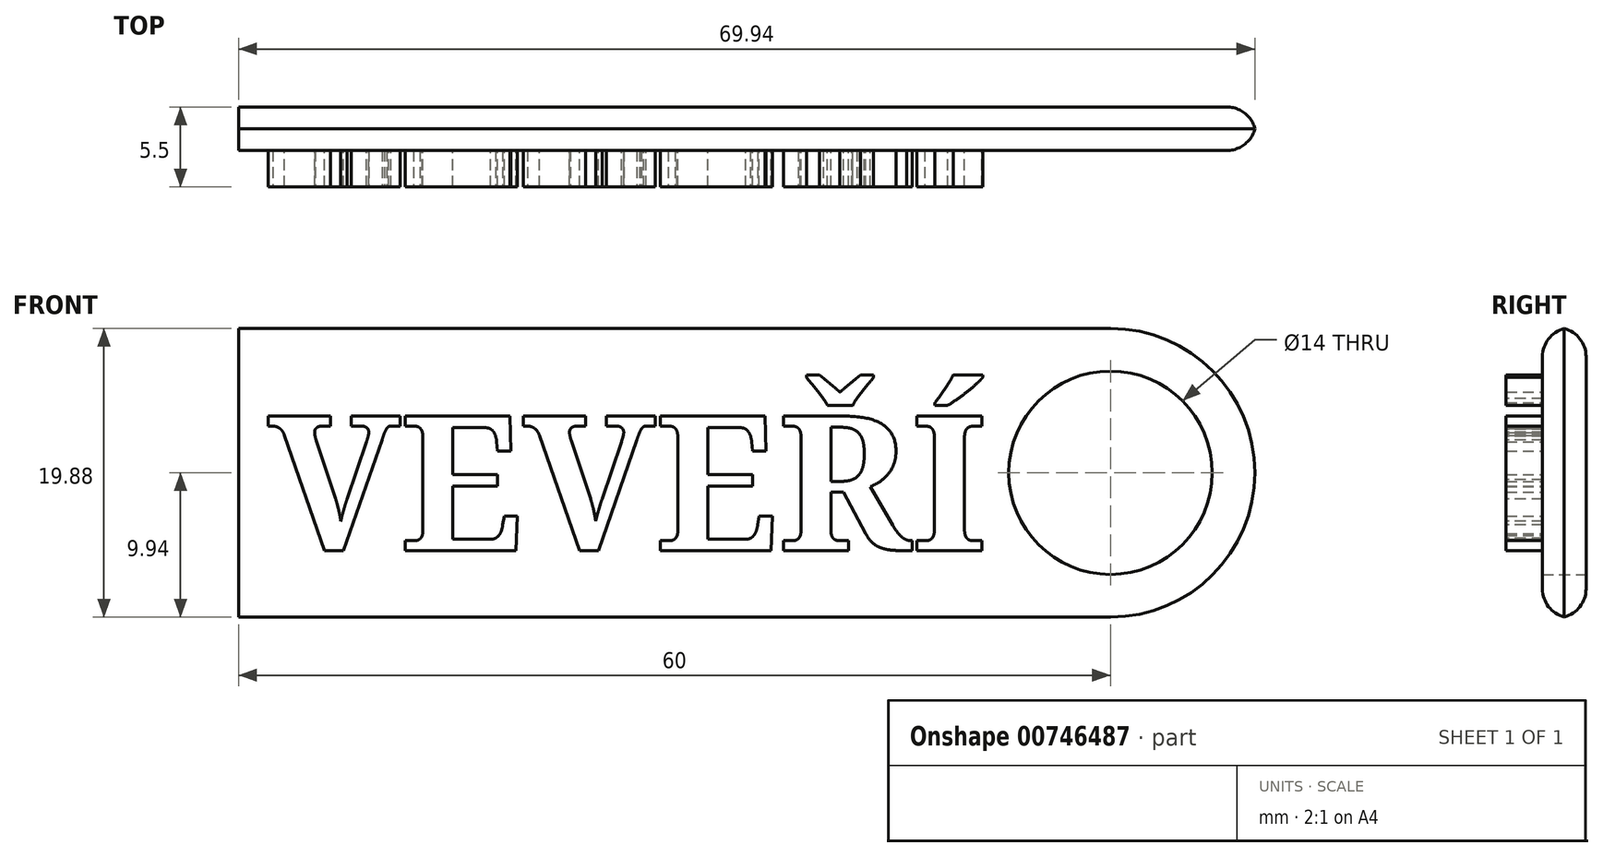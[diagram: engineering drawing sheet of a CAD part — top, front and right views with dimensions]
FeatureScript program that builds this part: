
annotation { "Feature Type Name" : "Feature", "Feature Type Description" : "" }
export const myFeature = defineFeature(function(context is Context, id is Id, definition is map)
    precondition{}
    {
        {
            var Q0;
            Q0=qCreatedBy(makeId("Front.planeOp"),FACE);
            var sketch = newSketch(context, id + "F0", { "sketchPlane" : qUnion([Q0])});
            skLineSegment(sketch, "E0.bottom", {"start": v(-30, 10) * mm, "end": v(30, 10) * mm});
            skLineSegment(sketch, "E0.top", {"start": v(-30, -10) * mm, "end": v(30, -10) * mm});
            skLineSegment(sketch, "E0.left", {"start": v(-30, 10) * mm, "end": v(-30, -10) * mm});
            skLineSegment(sketch, "E0.right", {"start": v(30, 10) * mm, "end": v(30, -10) * mm});
            skPoint(sketch, "E0.middle", {"position": v(0, 0) * mm});
            skCircle(sketch, "E1", {"center": v(30, 0) * mm, "radius": 10 * mm});
            skCircle(sketch, "E2.0", {"center": v(30, 0) * mm, "radius": 7 * mm});
            skSolve(sketch);
        }
        {
            var Q0;
            Q0 = qSketchRegion(id + "F0", true);
            extrude(context, id + "F1", {"entities" : qUnion([Q0]), "endBound" : BoundingType.SYMMETRIC, "depth" : 3 * mm, "offsetDistance" : 25 * mm});
        }
        {
            var Q0;
            Q0=makeQuery(id+"F1.opExtrude","CAP_EDGE",EDGE,{"disambiguationData":[OSD([sQuery(id+"F0.wireOp",EDGE,"E0.bottom")])],"isStart":true});
            var Q1;
            Q1=makeQuery(id+"F1.opExtrude","CAP_EDGE",EDGE,{"disambiguationData":[OSD([sQuery(id+"F0.wireOp",EDGE,"E0.bottom")])],"isStart":false});
            fillet(context, id + "F2", {"entities" : qUnion([Q0, Q1]), "radius" : 2 * mm, "tangentPropagation" : true, "allowEdgeOverflow" : false});
        }
        {
            var Q0;
            Q0=qCreatedBy(makeId("Front.planeOp"),FACE);
            var sketch = newSketch(context, id + "F3", { "sketchPlane" : qUnion([Q0])});
            skText(sketch, "E3", { "text": "VEVEŘÍ", "fontName": "NotoSerif-Bold.ttf"});
            const initialGuessF3  = {"E3": [-0.02796, -0.00537, 1, 0, 0.00935]};
            skSetInitialGuess(sketch, initialGuessF3);
            skSolve(sketch);
        }
        {
            var Q0;
            Q0 = qSketchRegion(id + "F3", true);
            extrude(context, id + "F4", {"entities" : qUnion([Q0]), "operationType" : NewBodyOperationType.ADD, "depth" : 4 * mm, "offsetDistance" : 25 * mm});
        }
    });
